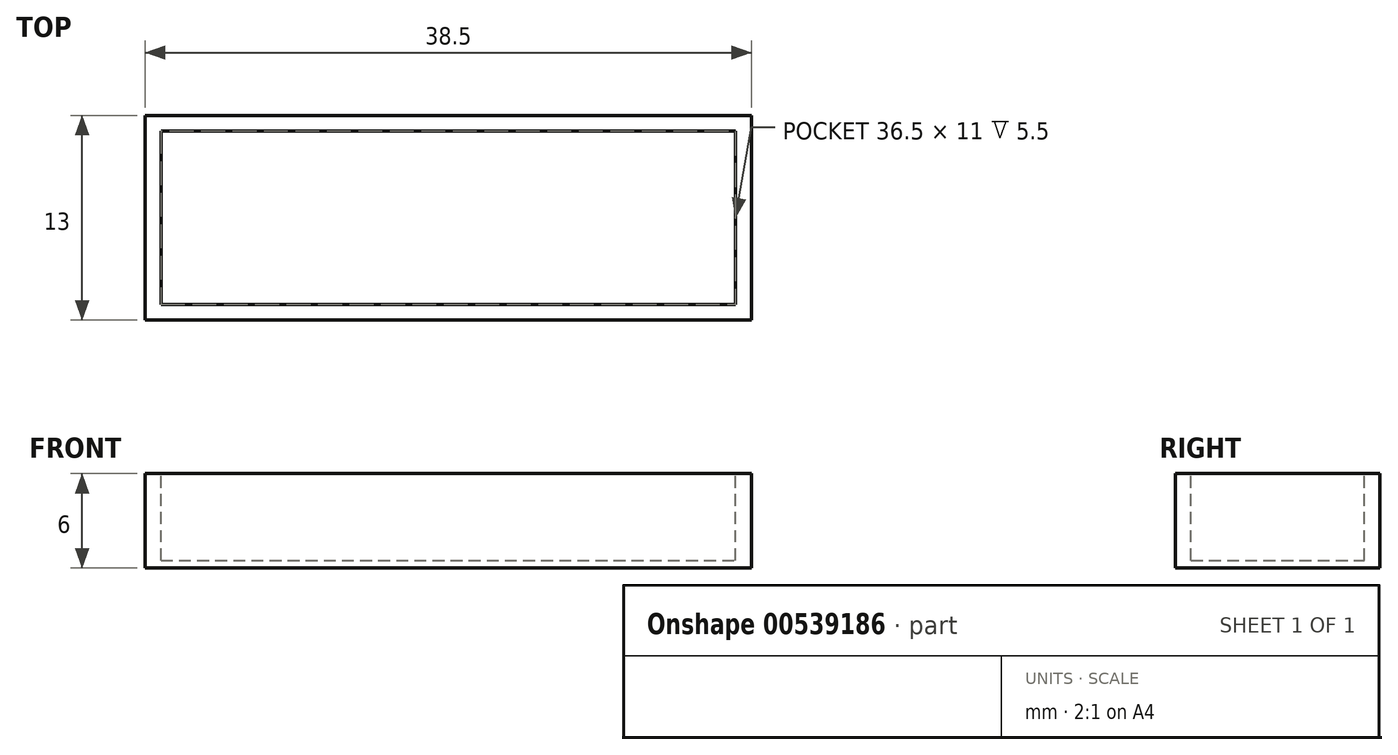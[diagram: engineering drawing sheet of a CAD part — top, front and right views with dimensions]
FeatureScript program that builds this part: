
annotation { "Feature Type Name" : "Feature", "Feature Type Description" : "" }
export const myFeature = defineFeature(function(context is Context, id is Id, definition is map)
    precondition{}
    {
        {
            var Q0;
            Q0=qCreatedBy(makeId("Top.planeOp"),FACE);
            var sketch = newSketch(context, id + "F0", { "sketchPlane" : qUnion([Q0])});
            skLineSegment(sketch, "E0.bottom", {"start": v(0, 0) * mm, "end": v(37.5, 0) * mm});
            skLineSegment(sketch, "E0.top", {"start": v(0, 12) * mm, "end": v(37.5, 12) * mm});
            skLineSegment(sketch, "E0.left", {"start": v(0, 0) * mm, "end": v(0, 12) * mm});
            skLineSegment(sketch, "E0.right", {"start": v(37.5, 0) * mm, "end": v(37.5, 12) * mm});
            skSolve(sketch);
        }
        {
            var Q0;
            Q0=qSketchRegion(id+"F0",true);
            extrude(context, id + "F1", {"entities" : qUnion([Q0]), "depth" : 6 * mm, "offsetDistance" : 25 * mm});
        }
        {
            var Q0;
            Q0=makeQuery(id+"F1.opExtrude","CAP_FACE",FACE,{"disambiguationData":[OSD([sQuery(id+"F0.wireOp",EDGE,"E0.bottom"),sQuery(id+"F0.wireOp",EDGE,"E0.top"),sQuery(id+"F0.wireOp",EDGE,"E0.left"),sQuery(id+"F0.wireOp",EDGE,"E0.right")])],"isStart":false});
            var sketch = newSketch(context, id + "F2", { "sketchPlane" : qUnion([Q0])});
            skLineSegment(sketch, "E1.bottom", {"start": v(0.5, 0.5) * mm, "end": v(37, 0.5) * mm});
            skLineSegment(sketch, "E1.top", {"start": v(0.5, 11.5) * mm, "end": v(37, 11.5) * mm});
            skLineSegment(sketch, "E1.left", {"start": v(0.5, 0.5) * mm, "end": v(0.5, 11.5) * mm});
            skLineSegment(sketch, "E1.right", {"start": v(37, 0.5) * mm, "end": v(37, 11.5) * mm});
            skSolve(sketch);
        }
        {
            var Q0;
            Q0=qSketchRegion(id+"F2",true);
            extrude(context, id + "F3", {"entities" : qUnion([Q0]), "operationType" : NewBodyOperationType.REMOVE, "oppositeDirection" : true, "depth" : 5.5 * mm, "offsetDistance" : 25 * mm});
        }
        {
            var Q0;
            Q0=makeQuery(id+"F1.opExtrude","CAP_FACE",FACE,{"disambiguationData":[OSD([sQuery(id+"F0.wireOp",EDGE,"E0.bottom"),sQuery(id+"F0.wireOp",EDGE,"E0.top"),sQuery(id+"F0.wireOp",EDGE,"E0.left"),sQuery(id+"F0.wireOp",EDGE,"E0.right")])],"isStart":true});
            var sketch = newSketch(context, id + "F4", { "sketchPlane" : qUnion([Q0])});
            skLineSegment(sketch, "E2.bottom", {"start": v(-0.5, -12.5) * mm, "end": v(38, -12.5) * mm});
            skLineSegment(sketch, "E2.top", {"start": v(-0.5, 0.5) * mm, "end": v(38, 0.5) * mm});
            skLineSegment(sketch, "E2.left", {"start": v(-0.5, -12.5) * mm, "end": v(-0.5, 0.5) * mm});
            skLineSegment(sketch, "E2.right", {"start": v(38, -12.5) * mm, "end": v(38, 0.5) * mm});
            skLineSegment(sketch, "E3.bottom", {"start": v(0, 0) * mm, "end": v(37.5, 0) * mm});
            skLineSegment(sketch, "E3.top", {"start": v(0, -12) * mm, "end": v(37.5, -12) * mm});
            skLineSegment(sketch, "E3.left", {"start": v(0, 0) * mm, "end": v(0, -12) * mm});
            skLineSegment(sketch, "E3.right", {"start": v(37.5, 0) * mm, "end": v(37.5, -12) * mm});
            skSolve(sketch);
        }
        {
            var Q0;
            Q0 = qSketchRegion(id + "F4", true);
            extrude(context, id + "F5", {"entities" : qUnion([Q0]), "operationType" : NewBodyOperationType.ADD, "oppositeDirection" : true, "depth" : 6 * mm, "offsetDistance" : 25 * mm});
        }
    });
